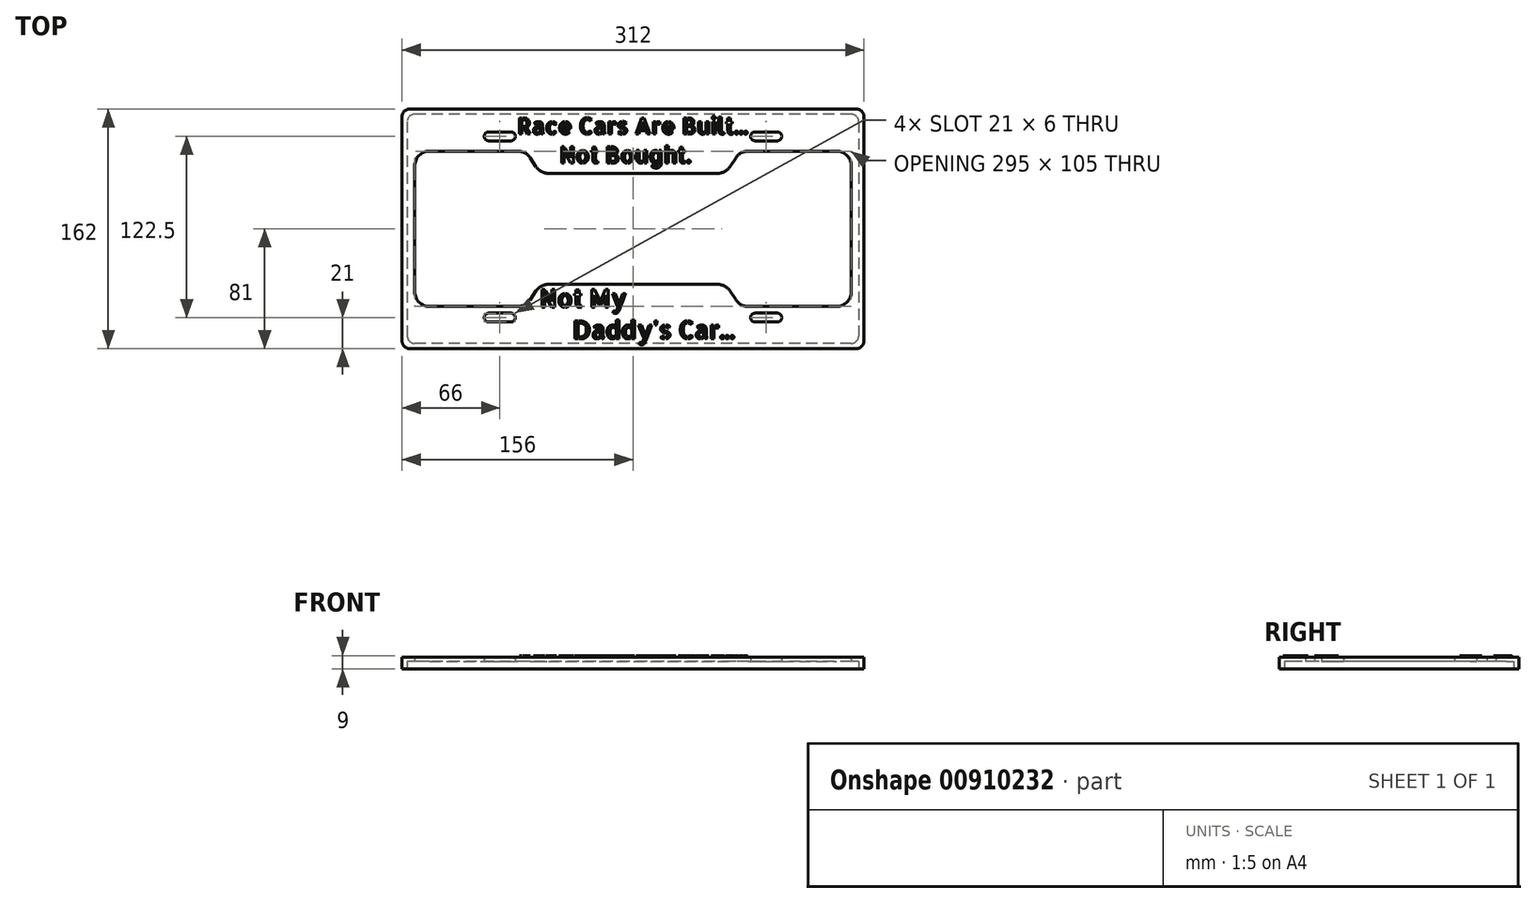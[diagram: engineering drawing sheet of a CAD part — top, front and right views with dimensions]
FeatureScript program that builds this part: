
annotation { "Feature Type Name" : "Feature", "Feature Type Description" : "" }
export const myFeature = defineFeature(function(context is Context, id is Id, definition is map)
    precondition{}
    {
        {
            var Q0;
            Q0=qCreatedBy(makeId("Top.planeOp"),FACE);
            var sketch = newSketch(context, id + "F0", { "sketchPlane" : qUnion([Q0])});
            skLineSegment(sketch, "E0.bottom", {"start": v(147.5, 77.5) * mm, "end": v(-147.5, 77.5) * mm});
            skLineSegment(sketch, "E0.top", {"start": v(147.5, -77.5) * mm, "end": v(-147.5, -77.5) * mm});
            skLineSegment(sketch, "E0.left", {"start": v(152.5, 72.5) * mm, "end": v(152.5, -72.5) * mm});
            skLineSegment(sketch, "E0.right", {"start": v(-152.5, 72.5) * mm, "end": v(-152.5, -72.5) * mm});
            skPoint(sketch, "E0.middle", {"position": v(0, 0) * mm});
            skLineSegment(sketch, "E1.bottom", {"start": v(151, 81) * mm, "end": v(-151, 81) * mm});
            skLineSegment(sketch, "E1.top", {"start": v(151, -81) * mm, "end": v(-151, -81) * mm});
            skLineSegment(sketch, "E1.left", {"start": v(156, 76) * mm, "end": v(156, -76) * mm});
            skLineSegment(sketch, "E1.right", {"start": v(-156, 76) * mm, "end": v(-156, -76) * mm});
            skArc(sketch, "E2", {"start": v(-97.5, 65.5) * mm, "mid": v(-100.5, 62.5) * mm, "end": v(-97.5, 59.5) * mm});
            skArc(sketch, "E3.1.0.0", {"start": v(-82.5, 59.5) * mm, "mid": v(-79.5, 62.5) * mm, "end": v(-82.5, 65.5) * mm});
            skLineSegment(sketch, "E3.direction1", {"start": v(-97.5, 62.5) * mm, "end": v(-82.5, 62.5) * mm, "construction": true});
            skLineSegment(sketch, "E4", {"start": v(-97.5, 65.5) * mm, "end": v(-82.5, 65.5) * mm});
            skLineSegment(sketch, "E5", {"start": v(-97.5, 59.5) * mm, "end": v(-82.5, 59.5) * mm});
            skLineSegment(sketch, "E6.0.1.0", {"start": v(-97.5, -63) * mm, "end": v(-82.5, -63) * mm});
            skArc(sketch, "E6.0.1.1", {"start": v(-82.5, -63) * mm, "mid": v(-79.5, -60) * mm, "end": v(-82.5, -57) * mm});
            skLineSegment(sketch, "E6.0.1.2", {"start": v(-97.5, -57) * mm, "end": v(-82.5, -57) * mm});
            skArc(sketch, "E6.0.1.3", {"start": v(-97.5, -57) * mm, "mid": v(-100.5, -60) * mm, "end": v(-97.5, -63) * mm});
            skLineSegment(sketch, "E6.0.1.4", {"start": v(-97.5, -60) * mm, "end": v(-82.5, -60) * mm, "construction": true});
            skLineSegment(sketch, "E6.1.0.0", {"start": v(82.5, 59.5) * mm, "end": v(97.5, 59.5) * mm});
            skArc(sketch, "E6.1.0.1", {"start": v(97.5, 59.5) * mm, "mid": v(100.5, 62.5) * mm, "end": v(97.5, 65.5) * mm});
            skLineSegment(sketch, "E6.1.0.2", {"start": v(82.5, 65.5) * mm, "end": v(97.5, 65.5) * mm});
            skArc(sketch, "E6.1.0.3", {"start": v(82.5, 65.5) * mm, "mid": v(79.5, 62.5) * mm, "end": v(82.5, 59.5) * mm});
            skLineSegment(sketch, "E6.1.0.4", {"start": v(82.5, 62.5) * mm, "end": v(97.5, 62.5) * mm, "construction": true});
            skLineSegment(sketch, "E6.1.1.0", {"start": v(82.5, -63) * mm, "end": v(97.5, -63) * mm});
            skArc(sketch, "E6.1.1.1", {"start": v(97.5, -63) * mm, "mid": v(100.5, -60) * mm, "end": v(97.5, -57) * mm});
            skLineSegment(sketch, "E6.1.1.2", {"start": v(82.5, -57) * mm, "end": v(97.5, -57) * mm});
            skArc(sketch, "E6.1.1.3", {"start": v(82.5, -57) * mm, "mid": v(79.5, -60) * mm, "end": v(82.5, -63) * mm});
            skLineSegment(sketch, "E6.1.1.4", {"start": v(82.5, -60) * mm, "end": v(97.5, -60) * mm, "construction": true});
            skLineSegment(sketch, "E6.direction1", {"start": v(-97.5, 59.5) * mm, "end": v(82.5, 59.5) * mm, "construction": true});
            skLineSegment(sketch, "E6.direction2", {"start": v(-97.5, 59.5) * mm, "end": v(-97.5, -63) * mm, "construction": true});
            skLineSegment(sketch, "E7", {"start": v(-137.5, -52.5) * mm, "end": v(-77.85, -52.5) * mm});
            skLineSegment(sketch, "E8", {"start": v(-69.53, -48.05) * mm, "end": v(-65.47, -41.95) * mm});
            skLineSegment(sketch, "E9", {"start": v(0, 0) * mm, "end": v(0, -123.14) * mm, "construction": true});
            skLineSegment(sketch, "E10.MirrorCS", {"start": v(69.53, -48.05) * mm, "end": v(65.47, -41.95) * mm});
            skLineSegment(sketch, "E11.trimOffspring", {"start": v(-57.15, -37.5) * mm, "end": v(57.15, -37.5) * mm});
            skLineSegment(sketch, "E12", {"start": v(0, 0) * mm, "end": v(225.83, 0) * mm, "construction": true});
            skLineSegment(sketch, "E13.trimOffspring", {"start": v(77.85, -52.5) * mm, "end": v(137.5, -52.5) * mm});
            skLineSegment(sketch, "E14.MirrorCS", {"start": v(-57.15, 37.5) * mm, "end": v(57.15, 37.5) * mm});
            skLineSegment(sketch, "E15.MirrorCS", {"start": v(69.53, 48.05) * mm, "end": v(65.47, 41.95) * mm});
            skLineSegment(sketch, "E16.MirrorCS", {"start": v(-69.53, 48.05) * mm, "end": v(-65.47, 41.95) * mm});
            skLineSegment(sketch, "E17.MirrorCS", {"start": v(-137.5, 52.5) * mm, "end": v(-77.85, 52.5) * mm});
            skLineSegment(sketch, "E18.MirrorCS", {"start": v(77.85, 52.5) * mm, "end": v(137.5, 52.5) * mm});
            skLineSegment(sketch, "E19", {"start": v(-147.5, 42.5) * mm, "end": v(-147.5, -42.5) * mm});
            skLineSegment(sketch, "E20.MirrorCS", {"start": v(147.5, 42.5) * mm, "end": v(147.5, -42.5) * mm});
            skPoint(sketch, "E21.visualSharp", {"position": v(-62.5, 37.5) * mm});
            skArc(sketch, "E21.filletArc", {"start": v(-65.47, 41.95) * mm, "mid": v(-61.87, 38.68) * mm, "end": v(-57.15, 37.5) * mm});
            skPoint(sketch, "E22.visualSharp", {"position": v(-72.5, 52.5) * mm});
            skArc(sketch, "E22.filletArc", {"start": v(-69.53, 48.05) * mm, "mid": v(-73.13, 51.32) * mm, "end": v(-77.85, 52.5) * mm});
            skPoint(sketch, "E23.visualSharp", {"position": v(62.5, 37.5) * mm});
            skArc(sketch, "E23.filletArc", {"start": v(57.15, 37.5) * mm, "mid": v(61.87, 38.68) * mm, "end": v(65.47, 41.95) * mm});
            skPoint(sketch, "E24.visualSharp", {"position": v(72.5, 52.5) * mm});
            skArc(sketch, "E24.filletArc", {"start": v(77.85, 52.5) * mm, "mid": v(73.13, 51.32) * mm, "end": v(69.53, 48.05) * mm});
            skPoint(sketch, "E25.visualSharp", {"position": v(72.5, -52.5) * mm});
            skArc(sketch, "E25.filletArc", {"start": v(69.53, -48.05) * mm, "mid": v(73.13, -51.32) * mm, "end": v(77.85, -52.5) * mm});
            skPoint(sketch, "E26.visualSharp", {"position": v(62.5, -37.5) * mm});
            skArc(sketch, "E26.filletArc", {"start": v(65.47, -41.95) * mm, "mid": v(61.87, -38.68) * mm, "end": v(57.15, -37.5) * mm});
            skPoint(sketch, "E27.visualSharp", {"position": v(-62.5, -37.5) * mm});
            skArc(sketch, "E27.filletArc", {"start": v(-57.15, -37.5) * mm, "mid": v(-61.87, -38.68) * mm, "end": v(-65.47, -41.95) * mm});
            skPoint(sketch, "E28.visualSharp", {"position": v(-72.5, -52.5) * mm});
            skArc(sketch, "E28.filletArc", {"start": v(-77.85, -52.5) * mm, "mid": v(-73.13, -51.32) * mm, "end": v(-69.53, -48.05) * mm});
            skPoint(sketch, "E29.visualSharp", {"position": v(-147.5, -52.5) * mm});
            skArc(sketch, "E29.filletArc", {"start": v(-147.5, -42.5) * mm, "mid": v(-144.57, -49.57) * mm, "end": v(-137.5, -52.5) * mm});
            skPoint(sketch, "E30.visualSharp", {"position": v(-147.5, 52.5) * mm});
            skArc(sketch, "E30.filletArc", {"start": v(-137.5, 52.5) * mm, "mid": v(-144.57, 49.57) * mm, "end": v(-147.5, 42.5) * mm});
            skPoint(sketch, "E31.visualSharp", {"position": v(147.5, 52.5) * mm});
            skArc(sketch, "E31.filletArc", {"start": v(147.5, 42.5) * mm, "mid": v(144.57, 49.57) * mm, "end": v(137.5, 52.5) * mm});
            skPoint(sketch, "E32.visualSharp", {"position": v(147.5, -52.5) * mm});
            skArc(sketch, "E32.filletArc", {"start": v(137.5, -52.5) * mm, "mid": v(144.57, -49.57) * mm, "end": v(147.5, -42.5) * mm});
            skPoint(sketch, "E33.visualSharp", {"position": v(-156, 81) * mm});
            skArc(sketch, "E33.filletArc", {"start": v(-151, 81) * mm, "mid": v(-154.54, 79.54) * mm, "end": v(-156, 76) * mm});
            skPoint(sketch, "E34.visualSharp", {"position": v(156, 81) * mm});
            skArc(sketch, "E34.filletArc", {"start": v(156, 76) * mm, "mid": v(154.54, 79.54) * mm, "end": v(151, 81) * mm});
            skPoint(sketch, "E35.visualSharp", {"position": v(156, -81) * mm});
            skArc(sketch, "E35.filletArc", {"start": v(151, -81) * mm, "mid": v(154.54, -79.54) * mm, "end": v(156, -76) * mm});
            skPoint(sketch, "E36.visualSharp", {"position": v(-156, -81) * mm});
            skArc(sketch, "E36.filletArc", {"start": v(-156, -76) * mm, "mid": v(-154.54, -79.54) * mm, "end": v(-151, -81) * mm});
            skPoint(sketch, "E37.visualSharp", {"position": v(-152.5, 77.5) * mm});
            skArc(sketch, "E37.filletArc", {"start": v(-147.5, 77.5) * mm, "mid": v(-151.04, 76.04) * mm, "end": v(-152.5, 72.5) * mm});
            skPoint(sketch, "E38.visualSharp", {"position": v(152.5, 77.5) * mm});
            skArc(sketch, "E38.filletArc", {"start": v(152.5, 72.5) * mm, "mid": v(151.04, 76.04) * mm, "end": v(147.5, 77.5) * mm});
            skPoint(sketch, "E39.visualSharp", {"position": v(152.5, -77.5) * mm});
            skArc(sketch, "E39.filletArc", {"start": v(147.5, -77.5) * mm, "mid": v(151.04, -76.04) * mm, "end": v(152.5, -72.5) * mm});
            skPoint(sketch, "E40.visualSharp", {"position": v(-152.5, -77.5) * mm});
            skArc(sketch, "E40.filletArc", {"start": v(-152.5, -72.5) * mm, "mid": v(-151.04, -76.04) * mm, "end": v(-147.5, -77.5) * mm});
            skSolve(sketch);
        }
        {
            var Q0;
            Q0=makeQuery(id+"F0.imprint","IMPRINT",FACE,{"disambiguationData":[TD([[makeQuery(id+"F0.imprint","IMPRINT",EDGE,{"derivedFrom":sQuery(id+"F0.wireOp",EDGE,"E0.bottom")}),-1.0]])]});
            var Q1;
            Q1=makeQuery(id+"F0.imprint","IMPRINT",FACE,{"disambiguationData":[TD([[makeQuery(id+"F0.imprint","IMPRINT",EDGE,{"derivedFrom":sQuery(id+"F0.wireOp",EDGE,"E0.bottom")}),1.0]])]});
            extrude(context, id + "F1", {"entities" : qUnion([Q0, Q1]), "depth" : 8 * mm, "offsetDistance" : 25 * mm});
        }
        {
            var Q0;
            Q0=makeQuery(id+"F0.imprint","IMPRINT",FACE,{"disambiguationData":[TD([[makeQuery(id+"F0.imprint","IMPRINT",EDGE,{"derivedFrom":sQuery(id+"F0.wireOp",EDGE,"E0.bottom")}),1.0]])]});
            extrude(context, id + "F2", {"entities" : qUnion([Q0]), "operationType" : NewBodyOperationType.REMOVE, "depth" : 5 * mm, "offsetDistance" : 25 * mm});
        }
        {
            var Q0;
            Q0=makeQuery(id+"F1.opExtrude","CAP_FACE",FACE,{"disambiguationData":[OSD([sQuery(id+"F0.wireOp",EDGE,"E1.bottom"),sQuery(id+"F0.wireOp",EDGE,"E1.top"),sQuery(id+"F0.wireOp",EDGE,"E1.left"),sQuery(id+"F0.wireOp",EDGE,"E1.right"),sQuery(id+"F0.wireOp",EDGE,"E2"),sQuery(id+"F0.wireOp",EDGE,"E3.1.0.0"),sQuery(id+"F0.wireOp",EDGE,"E4"),sQuery(id+"F0.wireOp",EDGE,"E5"),sQuery(id+"F0.wireOp",EDGE,"E6.0.1.0"),sQuery(id+"F0.wireOp",EDGE,"E6.0.1.1"),sQuery(id+"F0.wireOp",EDGE,"E6.0.1.2"),sQuery(id+"F0.wireOp",EDGE,"E6.0.1.3"),sQuery(id+"F0.wireOp",EDGE,"E6.1.0.0"),sQuery(id+"F0.wireOp",EDGE,"E6.1.0.1"),sQuery(id+"F0.wireOp",EDGE,"E6.1.0.2"),sQuery(id+"F0.wireOp",EDGE,"E6.1.0.3"),sQuery(id+"F0.wireOp",EDGE,"E6.1.1.0"),sQuery(id+"F0.wireOp",EDGE,"E6.1.1.1"),sQuery(id+"F0.wireOp",EDGE,"E6.1.1.2"),sQuery(id+"F0.wireOp",EDGE,"E6.1.1.3"),sQuery(id+"F0.wireOp",EDGE,"E7"),sQuery(id+"F0.wireOp",EDGE,"E8"),sQuery(id+"F0.wireOp",EDGE,"E10.MirrorCS"),sQuery(id+"F0.wireOp",EDGE,"E11.trimOffspring"),sQuery(id+"F0.wireOp",EDGE,"E13.trimOffspring"),sQuery(id+"F0.wireOp",EDGE,"E14.MirrorCS"),sQuery(id+"F0.wireOp",EDGE,"E15.MirrorCS"),sQuery(id+"F0.wireOp",EDGE,"E16.MirrorCS"),sQuery(id+"F0.wireOp",EDGE,"E17.MirrorCS"),sQuery(id+"F0.wireOp",EDGE,"E18.MirrorCS"),sQuery(id+"F0.wireOp",EDGE,"E19"),sQuery(id+"F0.wireOp",EDGE,"E20.MirrorCS"),sQuery(id+"F0.wireOp",EDGE,"E21.filletArc"),sQuery(id+"F0.wireOp",EDGE,"E22.filletArc"),sQuery(id+"F0.wireOp",EDGE,"E23.filletArc"),sQuery(id+"F0.wireOp",EDGE,"E24.filletArc"),sQuery(id+"F0.wireOp",EDGE,"E25.filletArc"),sQuery(id+"F0.wireOp",EDGE,"E26.filletArc"),sQuery(id+"F0.wireOp",EDGE,"E27.filletArc"),sQuery(id+"F0.wireOp",EDGE,"E28.filletArc"),sQuery(id+"F0.wireOp",EDGE,"E29.filletArc"),sQuery(id+"F0.wireOp",EDGE,"E30.filletArc"),sQuery(id+"F0.wireOp",EDGE,"E31.filletArc"),sQuery(id+"F0.wireOp",EDGE,"E32.filletArc"),sQuery(id+"F0.wireOp",EDGE,"E33.filletArc"),sQuery(id+"F0.wireOp",EDGE,"E34.filletArc"),sQuery(id+"F0.wireOp",EDGE,"E35.filletArc"),sQuery(id+"F0.wireOp",EDGE,"E36.filletArc")])],"isStart":false});
            var sketch = newSketch(context, id + "F3", { "sketchPlane" : qUnion([Q0])});
            skText(sketch, "E41", { "text": "Not My \n     Daddy\'s Car...", "fontName": "AllertaStencil-Regular.ttf"});
            const initialGuessF3  = {"E41": [-0.063, -0.053, 1, 0, 0.012]};
            skSetInitialGuess(sketch, initialGuessF3);
            skSolve(sketch);
        }
        {
            var Q0;
            Q0 = qSketchRegion(id + "F3", true);
            extrude(context, id + "F4", {"entities" : qUnion([Q0]), "operationType" : NewBodyOperationType.ADD, "depth" : 1 * mm, "offsetDistance" : 25 * mm});
        }
        {
            var Q0;
            Q0=makeQuery(id+"F1.opExtrude","CAP_FACE",FACE,{"disambiguationData":[OSD([sQuery(id+"F0.wireOp",EDGE,"E1.bottom"),sQuery(id+"F0.wireOp",EDGE,"E1.top"),sQuery(id+"F0.wireOp",EDGE,"E1.left"),sQuery(id+"F0.wireOp",EDGE,"E1.right"),sQuery(id+"F0.wireOp",EDGE,"E2"),sQuery(id+"F0.wireOp",EDGE,"E3.1.0.0"),sQuery(id+"F0.wireOp",EDGE,"E4"),sQuery(id+"F0.wireOp",EDGE,"E5"),sQuery(id+"F0.wireOp",EDGE,"E6.0.1.0"),sQuery(id+"F0.wireOp",EDGE,"E6.0.1.1"),sQuery(id+"F0.wireOp",EDGE,"E6.0.1.2"),sQuery(id+"F0.wireOp",EDGE,"E6.0.1.3"),sQuery(id+"F0.wireOp",EDGE,"E6.1.0.0"),sQuery(id+"F0.wireOp",EDGE,"E6.1.0.1"),sQuery(id+"F0.wireOp",EDGE,"E6.1.0.2"),sQuery(id+"F0.wireOp",EDGE,"E6.1.0.3"),sQuery(id+"F0.wireOp",EDGE,"E6.1.1.0"),sQuery(id+"F0.wireOp",EDGE,"E6.1.1.1"),sQuery(id+"F0.wireOp",EDGE,"E6.1.1.2"),sQuery(id+"F0.wireOp",EDGE,"E6.1.1.3"),sQuery(id+"F0.wireOp",EDGE,"E7"),sQuery(id+"F0.wireOp",EDGE,"E8"),sQuery(id+"F0.wireOp",EDGE,"E10.MirrorCS"),sQuery(id+"F0.wireOp",EDGE,"E11.trimOffspring"),sQuery(id+"F0.wireOp",EDGE,"E13.trimOffspring"),sQuery(id+"F0.wireOp",EDGE,"E14.MirrorCS"),sQuery(id+"F0.wireOp",EDGE,"E15.MirrorCS"),sQuery(id+"F0.wireOp",EDGE,"E16.MirrorCS"),sQuery(id+"F0.wireOp",EDGE,"E17.MirrorCS"),sQuery(id+"F0.wireOp",EDGE,"E18.MirrorCS"),sQuery(id+"F0.wireOp",EDGE,"E19"),sQuery(id+"F0.wireOp",EDGE,"E20.MirrorCS"),sQuery(id+"F0.wireOp",EDGE,"E21.filletArc"),sQuery(id+"F0.wireOp",EDGE,"E22.filletArc"),sQuery(id+"F0.wireOp",EDGE,"E23.filletArc"),sQuery(id+"F0.wireOp",EDGE,"E24.filletArc"),sQuery(id+"F0.wireOp",EDGE,"E25.filletArc"),sQuery(id+"F0.wireOp",EDGE,"E26.filletArc"),sQuery(id+"F0.wireOp",EDGE,"E27.filletArc"),sQuery(id+"F0.wireOp",EDGE,"E28.filletArc"),sQuery(id+"F0.wireOp",EDGE,"E29.filletArc"),sQuery(id+"F0.wireOp",EDGE,"E30.filletArc"),sQuery(id+"F0.wireOp",EDGE,"E31.filletArc"),sQuery(id+"F0.wireOp",EDGE,"E32.filletArc"),sQuery(id+"F0.wireOp",EDGE,"E33.filletArc"),sQuery(id+"F0.wireOp",EDGE,"E34.filletArc"),sQuery(id+"F0.wireOp",EDGE,"E35.filletArc"),sQuery(id+"F0.wireOp",EDGE,"E36.filletArc")])],"isStart":false});
            var sketch = newSketch(context, id + "F5", { "sketchPlane" : qUnion([Q0])});
            skText(sketch, "E42", { "text": "Race Cars Are Built...\n       Not Bought.", "fontName": "AllertaStencil-Regular.ttf"});
            const initialGuessF5  = {"E42": [-0.07824, 0.064, 1, 0, 0.011]};
            skSetInitialGuess(sketch, initialGuessF5);
            skSolve(sketch);
        }
        {
            var Q0;
            Q0 = qSketchRegion(id + "F5", true);
            extrude(context, id + "F6", {"entities" : qUnion([Q0]), "operationType" : NewBodyOperationType.ADD, "depth" : 1 * mm, "offsetDistance" : 25 * mm});
        }
    });
